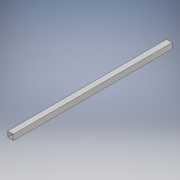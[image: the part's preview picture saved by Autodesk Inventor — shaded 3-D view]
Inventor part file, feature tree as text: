
AUTODESK INVENTOR PART (.ipt)
format: ipt  version: 2018 (Build 220112000, 112)  size: 97,792 bytes
history: native  units: in
note: dims shown in document units (in); Inventor stores cm internally (conversion verified against a paired STEP export)
features: extrude x1, sketch x1
ambient origin geometry x8: Origin, YZ Plane, XZ Plane, XY Plane, X Axis, Y Axis, Z Axis, Center Point
bodies: Solid1 (feature_tree)
feature tree (2):
  extrude  "Extrusion1"  Depth=1.0in
  sketch  "Sketch1"  dims[d0=1.0in d1=1.0in d2=0.125in d3=28.0in d4=0.0in]
